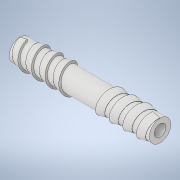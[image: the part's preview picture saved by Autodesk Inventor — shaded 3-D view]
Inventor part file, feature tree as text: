
AUTODESK INVENTOR PART (.ipt)
format: ipt  version: 2020.2 (Build 242310000, 310)  size: 238,592 bytes
history: native  units: mm
features: sketch x4, extrude x3, other x2, mirror x1, projected_geometry x1
ambient origin geometry x8: Origin, YZ Plane, XZ Plane, XY Plane, X Axis, Y Axis, Z Axis, Center Point
bodies: Volumenkörper1 (feature_tree), Solid2 (feature_tree), Solid3 (feature_tree)
feature tree (11):
  other  "Dribblerschnecke"
  extrude  "Extrusion1"  Depth=11.0mm
  other  "Spirale1"
  mirror  "Spiegeln1"
  extrude  "Extrusion5"  Depth=10.0mm
  extrude  "Extrusion6"  Depth=7.0mm
  sketch  "Skizze1"  dims[d0=6.0mm d1=11.0mm]
  sketch  "Skizze3"  dims[d2=36.0mm d3=0.0mm]
  projected_geometry  "Projizierte Kontur2"
  sketch  "Sketch7"  dims[d8=7.0mm d9=24.5mm d10=10.0mm d11=0.0mm d12=90.0deg d13=90.0deg d14=0.0mm d15=0.0mm d16=4.0mm]
  sketch  "Sketch8"  dims[d17=13.962634mm d18=1.0mm d19=0.1mm d32=10.0mm d33=0.0mm d34=7.0mm d35=100.0mm d36=0.0mm d37=82.0mm d38=0.0mm]
